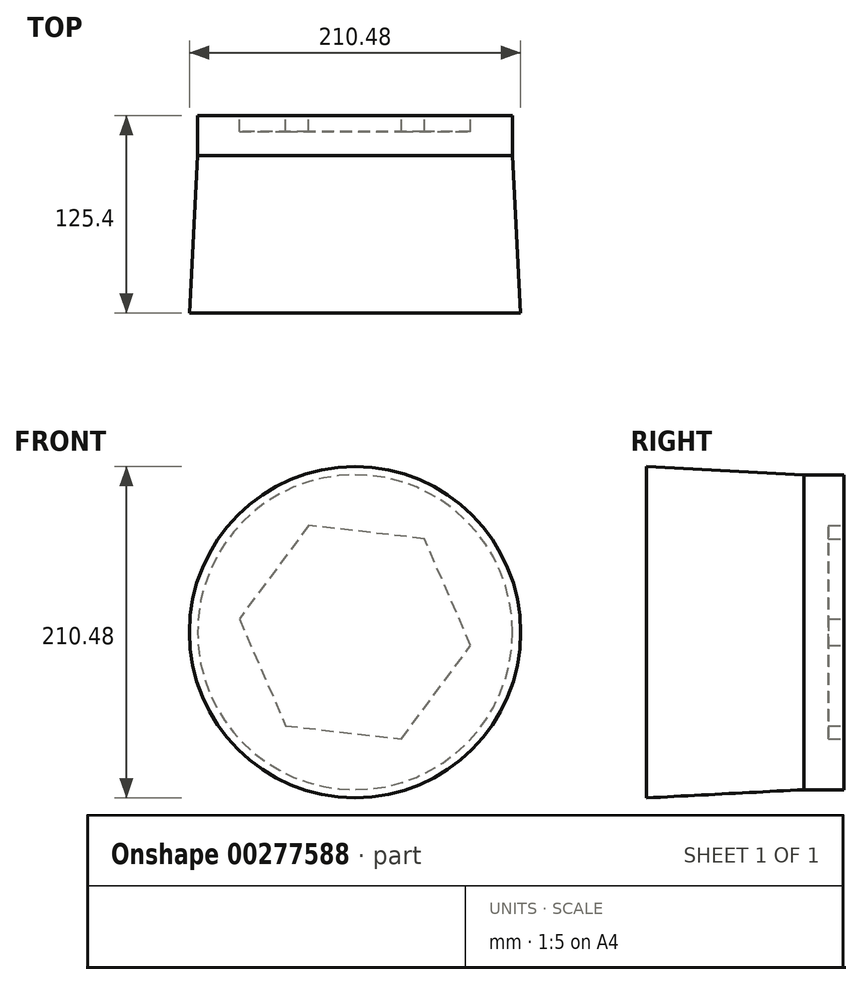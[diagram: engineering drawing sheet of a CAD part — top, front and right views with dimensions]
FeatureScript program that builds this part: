
annotation { "Feature Type Name" : "Feature", "Feature Type Description" : "" }
export const myFeature = defineFeature(function(context is Context, id is Id, definition is map)
    precondition{}
    {
        {
            var Q0;
            Q0=qCreatedBy(makeId("Front.planeOp"),FACE);
            var sketch = newSketch(context, id + "F0", { "sketchPlane" : qUnion([Q0])});
            skCircle(sketch, "E0", {"center": v(0, 0) * mm, "radius": 100 * mm});
            skSolve(sketch);
        }
        {
            var Q0;
            Q0=makeQuery(id+"F0.imprint","IMPRINT",FACE,{"disambiguationData":[TD([[makeQuery(id+"F0.imprint","IMPRINT",EDGE,{"derivedFrom":sQuery(id+"F0.wireOp",EDGE,"E0")}),1.0]])]});
            extrude(context, id + "F1", {"entities" : qUnion([Q0]), "depth" : 100 * mm, "hasDraft" : true, "draftAngle" : 3 * degree, "hasSecondDirection" : true, "secondDirectionOppositeDirection" : true, "secondDirectionDepth" : 25.4 * mm});
        }
        {
            var Q0;
            Q0=makeQuery(id+"F1.opExtrude","CAP_FACE",FACE,{"disambiguationData":[OSD([sQuery(id+"F0.wireOp",EDGE,"E0")])],"isStart":true});
            var sketch = newSketch(context, id + "F2", { "sketchPlane" : qUnion([Q0])});
            skCircle(sketch, "E1.cCircle", {"center": v(0, 0) * mm, "radius": 64.04 * mm, "construction": true});
            skLineSegment(sketch, "E1.0", {"start": v(-73.46, -8.46) * mm, "end": v(-44.06, 59.39) * mm});
            skLineSegment(sketch, "E1.1", {"start": v(-44.06, 59.39) * mm, "end": v(29.4, 67.85) * mm});
            skLineSegment(sketch, "E1.2", {"start": v(29.4, 67.85) * mm, "end": v(73.46, 8.46) * mm});
            skLineSegment(sketch, "E1.3", {"start": v(73.46, 8.46) * mm, "end": v(44.06, -59.39) * mm});
            skLineSegment(sketch, "E1.4", {"start": v(44.06, -59.39) * mm, "end": v(-29.4, -67.85) * mm});
            skLineSegment(sketch, "E1.5", {"start": v(-29.4, -67.85) * mm, "end": v(-73.46, -8.46) * mm});
            skPoint(sketch, "E1.0.midPoint", {"position": v(-58.76, 25.46) * mm});
            skSolve(sketch);
        }
        {
            var Q0;
            Q0 = qSketchRegion(id + "F2", true);
            extrude(context, id + "F3", {"entities" : qUnion([Q0]), "operationType" : NewBodyOperationType.REMOVE, "oppositeDirection" : true, "depth" : 10 * mm});
        }
    });
